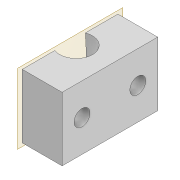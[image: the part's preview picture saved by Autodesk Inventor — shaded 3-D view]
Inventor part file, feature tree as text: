
AUTODESK INVENTOR PART (.ipt)
format: ipt  version: 2022 (Build 260153000, 153)  size: 124,416 bytes
history: native  units: mm
features: extrude x4, sketch x4, plane x1, projected_geometry x1
ambient origin geometry x8: Origin, YZ Plane, XZ Plane, XY Plane, X Axis, Y Axis, Z Axis, Center Point
bodies: Solid1 (feature_tree)
feature tree (10):
  extrude  "Extrusion1"  Depth=5.0mm
  plane  "Work Plane1"
  extrude  "Extrusion2"  Depth=6.0mm
  extrude  "Extrusion3"  Depth=5.0mm
  extrude  "Extrusion4"  Depth=10.0mm
  sketch  "Sketch1"  dims[d0=4.0mm d2=5.0mm]
  sketch  "Sketch4"  dims[d3=6.0mm d4=6.0mm]
  sketch  "Sketch5"  dims[d5=8.0mm d6=0.0mm d7=5.0mm]
  projected_geometry  "Projected Loop1"
  sketch  "Sketch6"  dims[d8=1.745329mm d9=4.1mm d10=100.0mm d11=0.0mm d12=4.2mm d13=2.0mm d14=2.0mm d15=2.5mm d16=2.5mm d17=4.0mm d18=4.0mm d19=100.0mm d20=0.0mm d21=10.0mm d22=0.0mm]
